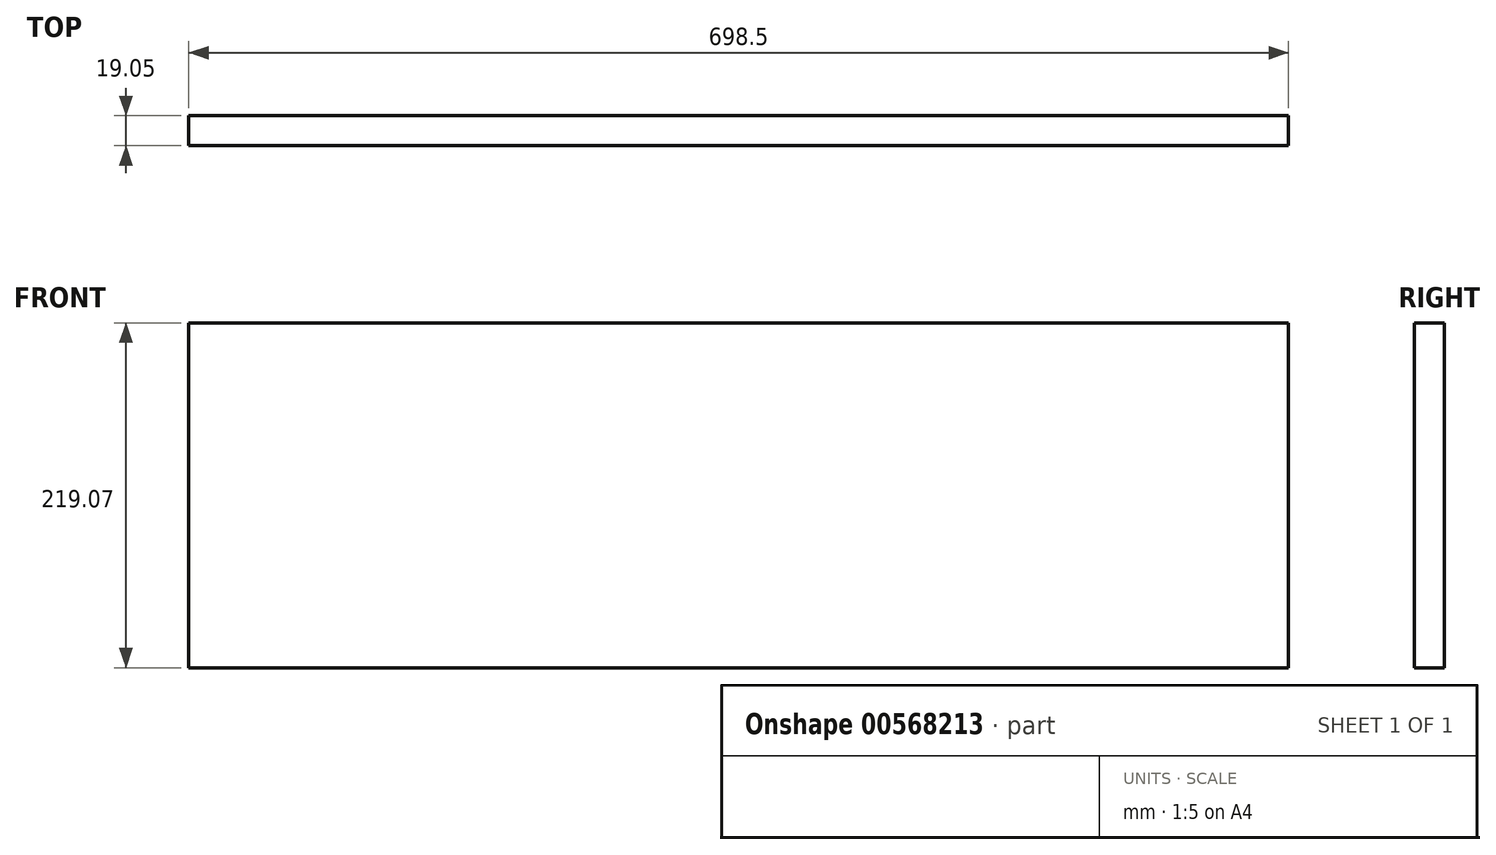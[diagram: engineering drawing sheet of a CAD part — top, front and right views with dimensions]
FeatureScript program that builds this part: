
annotation { "Feature Type Name" : "Feature", "Feature Type Description" : "" }
export const myFeature = defineFeature(function(context is Context, id is Id, definition is map)
    precondition{}
    {
        {
            var Q0;
            Q0=qCreatedBy(makeId("Front.planeOp"),FACE);
            var sketch = newSketch(context, id + "F0", { "sketchPlane" : qUnion([Q0])});
            skLineSegment(sketch, "E0.bottom", {"start": v(0, 0) * mm, "end": v(698.5, 0) * mm});
            skLineSegment(sketch, "E0.top", {"start": v(0, 219.08) * mm, "end": v(698.5, 219.08) * mm});
            skLineSegment(sketch, "E0.left", {"start": v(0, 0) * mm, "end": v(0, 219.08) * mm});
            skLineSegment(sketch, "E0.right", {"start": v(698.5, 0) * mm, "end": v(698.5, 219.08) * mm});
            skSolve(sketch);
        }
        {
            var Q0;
            Q0=makeQuery(id+"F0.imprint","IMPRINT",FACE,{"disambiguationData":[TD([[makeQuery(id+"F0.imprint","IMPRINT",EDGE,{"derivedFrom":sQuery(id+"F0.wireOp",EDGE,"E0.bottom")}),1.0]])]});
            extrude(context, id + "F1", {"entities" : qUnion([Q0]), "depth" : 19.05 * mm, "offsetDistance" : 25.4 * mm});
        }
    });
